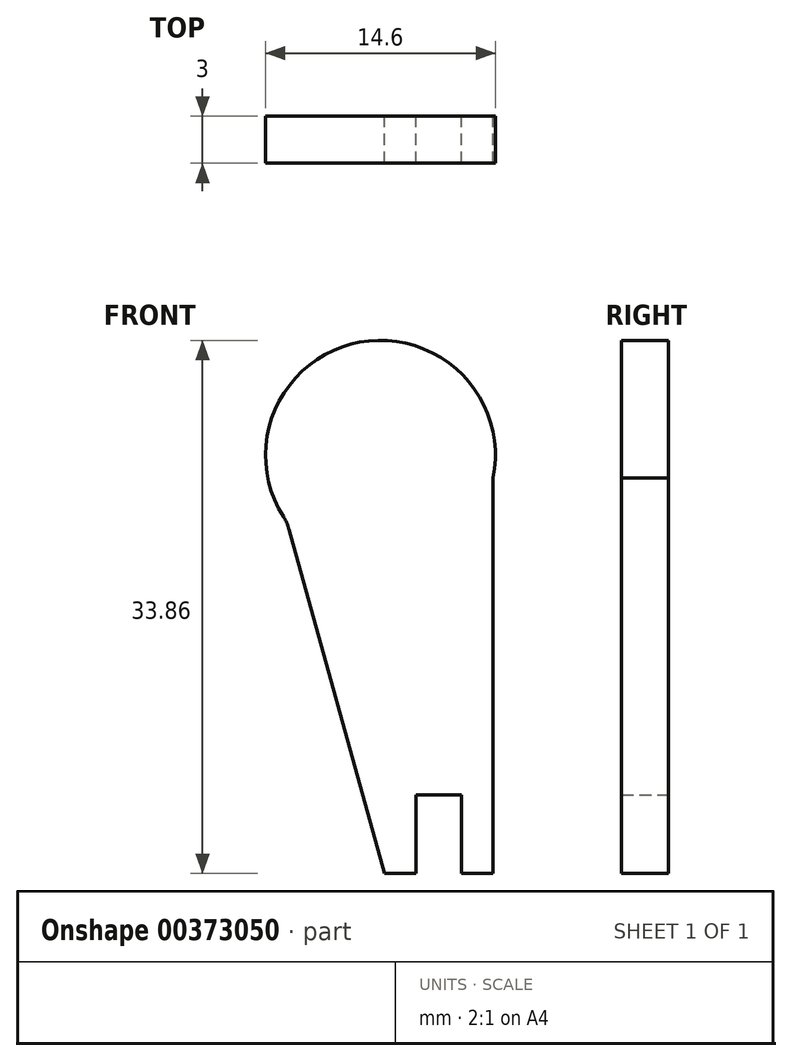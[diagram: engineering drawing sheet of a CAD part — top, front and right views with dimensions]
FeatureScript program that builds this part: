
annotation { "Feature Type Name" : "Feature", "Feature Type Description" : "" }
export const myFeature = defineFeature(function(context is Context, id is Id, definition is map)
    precondition{}
    {
        {
            var Q0;
            Q0=qCreatedBy(makeId("Front.planeOp"),FACE);
            var sketch = newSketch(context, id + "F0", { "sketchPlane" : qUnion([Q0])});
            skLineSegment(sketch, "E0", {"start": v(-19.27, 21.86) * mm, "end": v(-13.21, 0) * mm});
            skLineSegment(sketch, "E1", {"start": v(-6.31, 0) * mm, "end": v(-6.31, 26.44) * mm});
            skArc(sketch, "E2", {"start": v(-6.31, 25.1) * mm, "mid": v(-14.78, 33.74) * mm, "end": v(-19.63, 22.66) * mm});
            skPoint(sketch, "E3.orphan", {"position": v(-20.61, 26.69) * mm});
            skLineSegment(sketch, "E4.top", {"start": v(-8.31, 5) * mm, "end": v(-11.21, 5) * mm});
            skLineSegment(sketch, "E4.left", {"start": v(-8.31, 0) * mm, "end": v(-8.31, 5) * mm});
            skLineSegment(sketch, "E4.right", {"start": v(-11.21, 0) * mm, "end": v(-11.21, 5) * mm});
            skPoint(sketch, "E5.visualSharp", {"position": v(-19.4, 22.32) * mm});
            skArc(sketch, "E5.filletArc", {"start": v(-19.27, 21.86) * mm, "mid": v(-19.42, 22.27) * mm, "end": v(-19.63, 22.66) * mm});
            skLineSegment(sketch, "E6", {"start": v(-13.21, 0) * mm, "end": v(-11.21, 0) * mm});
            skLineSegment(sketch, "E7", {"start": v(-8.31, 0) * mm, "end": v(-6.31, 0) * mm});
            skSolve(sketch);
        }
        {
            var Q0;
            Q0=makeQuery(id+"F0.imprint","IMPRINT",FACE,{"disambiguationData":[TD([[makeQuery(id+"F0.imprint","IMPRINT",EDGE,{"derivedFrom":sQuery(id+"F0.wireOp",EDGE,"E4.bottom")}),-1.0]])]});
            var sketch = newSketch(context, id + "F1", { "sketchPlane" : qUnion([Q0])});
            skSolve(sketch);
        }
        {
            var Q0;
            Q0 = qSketchRegion(id + "F0", true);
            extrude(context, id + "F2", {"entities" : qUnion([Q0]), "depth" : 3 * mm});
        }
    });
